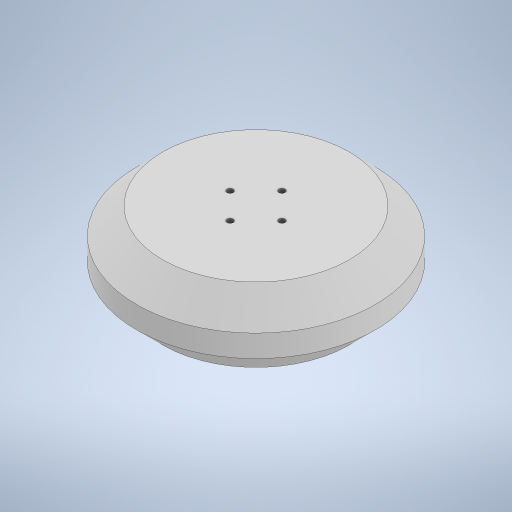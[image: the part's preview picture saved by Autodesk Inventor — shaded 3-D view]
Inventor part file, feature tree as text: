
AUTODESK INVENTOR PART (.ipt)
format: ipt  version: 2023 (Build 270158030, 158C)  size: 242,688 bytes
history: native  units: in
note: dims shown in document units (in); Inventor stores cm internally (conversion verified against a paired STEP export)
features: sketch x3, extrude x2, chamfer x1, hole x1
ambient origin geometry x8: Origin, YZ Plane, XZ Plane, XY Plane, X Axis, Y Axis, Z Axis, Center Point
bodies: Solid1 (feature_tree)
feature tree (7):
  extrude  "Extrusion1"  Depth=0.3937in
  chamfer  "Chamfer1"  Distance=0.3937in Angle=45.0deg
  hole  "Hole1"  [1 undecoded]
  extrude  "Extrusion2"  Depth=0.1969in TaperAngle=0.0deg
  sketch  "Sketch1"  dims[d0=1.122in d1=0.0in d2=3.622in d3=0.3937in d4=0.0787in d5=45.0deg]
  sketch  "Sketch2"  dims[d6=0.0968in d7=0.2362in d8=0.1575in d9=0.0787in d10=90.0deg d11=0.3465in d12=0.8108in d13=0.7874in]
  sketch  "Sketch3"  dims[d14=0.1969in d15=0.1969in d16=0.0in]
note: 1 required parameter value undecoded (feature->parameter linkage not recoverable at this tier; creation-order binding heuristic only, values carry confidence <= 0.55)
